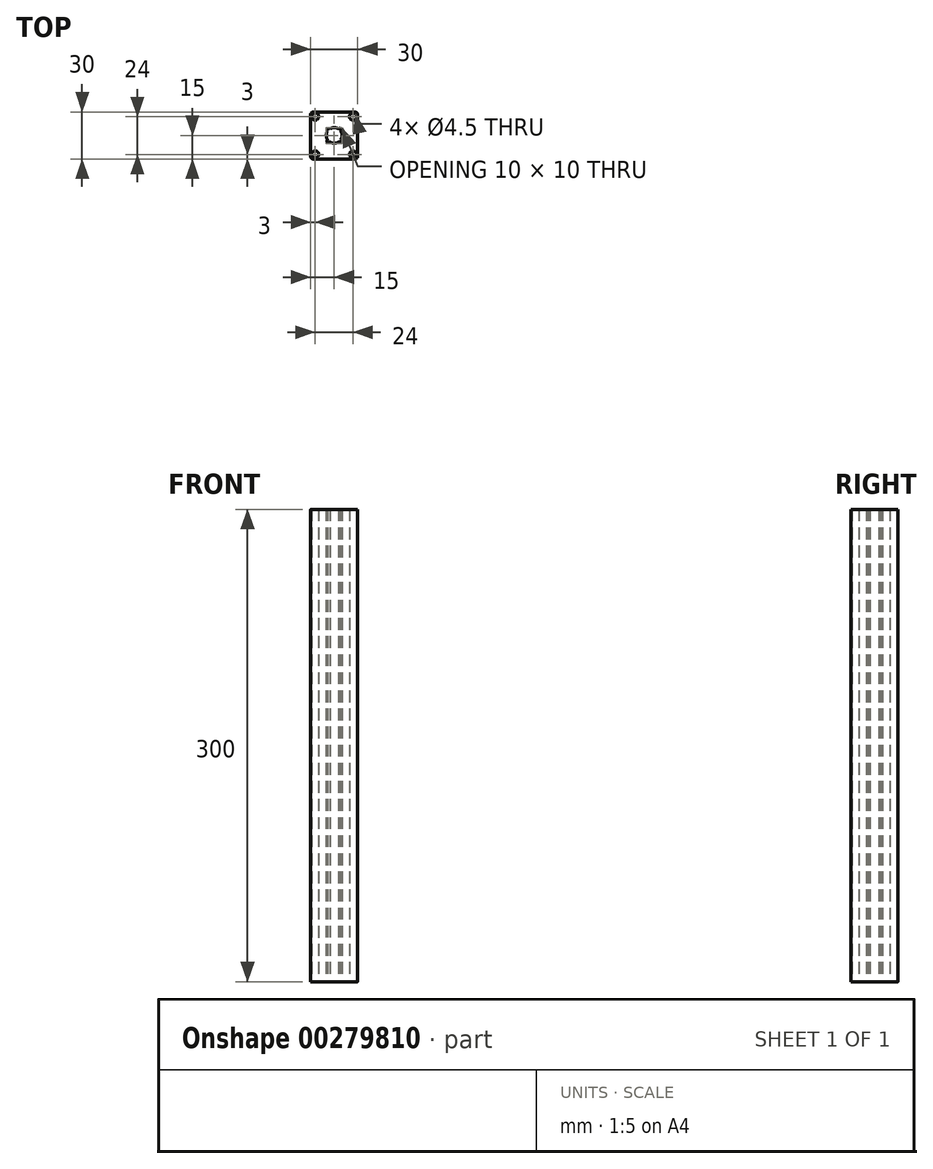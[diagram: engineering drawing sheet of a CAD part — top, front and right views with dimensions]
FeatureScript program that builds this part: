
annotation { "Feature Type Name" : "Feature", "Feature Type Description" : "" }
export const myFeature = defineFeature(function(context is Context, id is Id, definition is map)
    precondition{}
    {
        {
            var Q0;
            Q0=qCreatedBy(makeId("Top.planeOp"),FACE);
            var sketch = newSketch(context, id + "F0", { "sketchPlane" : qUnion([Q0])});
            skLineSegment(sketch, "E0.bottom", {"start": v(15, 15) * mm, "end": v(-15, 15) * mm});
            skLineSegment(sketch, "E0.top", {"start": v(15, -15) * mm, "end": v(-15, -15) * mm});
            skLineSegment(sketch, "E0.left", {"start": v(15, 15) * mm, "end": v(15, -15) * mm});
            skLineSegment(sketch, "E0.right", {"start": v(-15, 15) * mm, "end": v(-15, -15) * mm});
            skPoint(sketch, "E0.middle", {"position": v(0, 0) * mm});
            skArc(sketch, "E1", {"start": v(4.17, -2.76) * mm, "mid": v(5, 0) * mm, "end": v(4.17, 2.76) * mm});
            skArc(sketch, "E2", {"start": v(-2.76, 4.17) * mm, "mid": v(-4.24, 4.24) * mm, "end": v(-4.17, 2.76) * mm});
            skArc(sketch, "E3", {"start": v(4.17, 2.76) * mm, "mid": v(4.24, 4.24) * mm, "end": v(2.76, 4.17) * mm});
            skArc(sketch, "E4", {"start": v(2.76, -4.17) * mm, "mid": v(4.24, -4.24) * mm, "end": v(4.17, -2.76) * mm});
            skArc(sketch, "E5", {"start": v(-4.17, -2.76) * mm, "mid": v(-4.24, -4.24) * mm, "end": v(-2.76, -4.17) * mm});
            skCircle(sketch, "E6", {"center": v(-12, 12) * mm, "radius": 2.25 * mm});
            skCircle(sketch, "E7", {"center": v(-12, -12) * mm, "radius": 2.25 * mm});
            skCircle(sketch, "E8", {"center": v(12, -12) * mm, "radius": 2.25 * mm});
            skCircle(sketch, "E9", {"center": v(12, 12) * mm, "radius": 2.25 * mm});
            skArc(sketch, "E10.trimOffspring", {"start": v(-2.76, -4.17) * mm, "mid": v(0, -5) * mm, "end": v(2.76, -4.17) * mm});
            skArc(sketch, "E11.trimOffspring", {"start": v(-4.17, 2.76) * mm, "mid": v(-5, 0) * mm, "end": v(-4.17, -2.76) * mm});
            skArc(sketch, "E12.trimOffspring", {"start": v(2.76, 4.17) * mm, "mid": v(0, 5) * mm, "end": v(-2.76, 4.17) * mm});
            skSolve(sketch);
        }
        {
            var Q0;
            Q0=makeQuery(id+"F0.imprint","IMPRINT",FACE,{"disambiguationData":[TD([[makeQuery(id+"F0.imprint","IMPRINT",EDGE,{"derivedFrom":sQuery(id+"F0.wireOp",EDGE,"E0.bottom")}),1.0]])]});
            extrude(context, id + "F1", {"entities" : qUnion([Q0]), "depth" : 300 * mm});
        }
        {
            var Q0;
            Q0=makeQuery(id+"F1.opExtrude","SWEPT_EDGE",EDGE,{"disambiguationData":[OSD([sQuery(id+"F0.wireOp",EDGE,"E0.bottom"),sQuery(id+"F0.wireOp",EDGE,"E0.left")])]});
            var Q1;
            Q1=makeQuery(id+"F1.opExtrude","SWEPT_EDGE",EDGE,{"disambiguationData":[OSD([sQuery(id+"F0.wireOp",EDGE,"E0.bottom"),sQuery(id+"F0.wireOp",EDGE,"E0.right")])]});
            var Q2;
            Q2=makeQuery(id+"F1.opExtrude","SWEPT_EDGE",EDGE,{"disambiguationData":[OSD([sQuery(id+"F0.wireOp",EDGE,"E0.top"),sQuery(id+"F0.wireOp",EDGE,"E0.right")])]});
            var Q3;
            Q3=makeQuery(id+"F1.opExtrude","SWEPT_EDGE",EDGE,{"disambiguationData":[OSD([sQuery(id+"F0.wireOp",EDGE,"E0.top"),sQuery(id+"F0.wireOp",EDGE,"E0.left")])]});
            fillet(context, id + "F2", {"entities" : qUnion([Q0, Q1, Q2, Q3]), "radius" : 2 * mm, "tangentPropagation" : true, "allowEdgeOverflow" : false});
        }
    });
